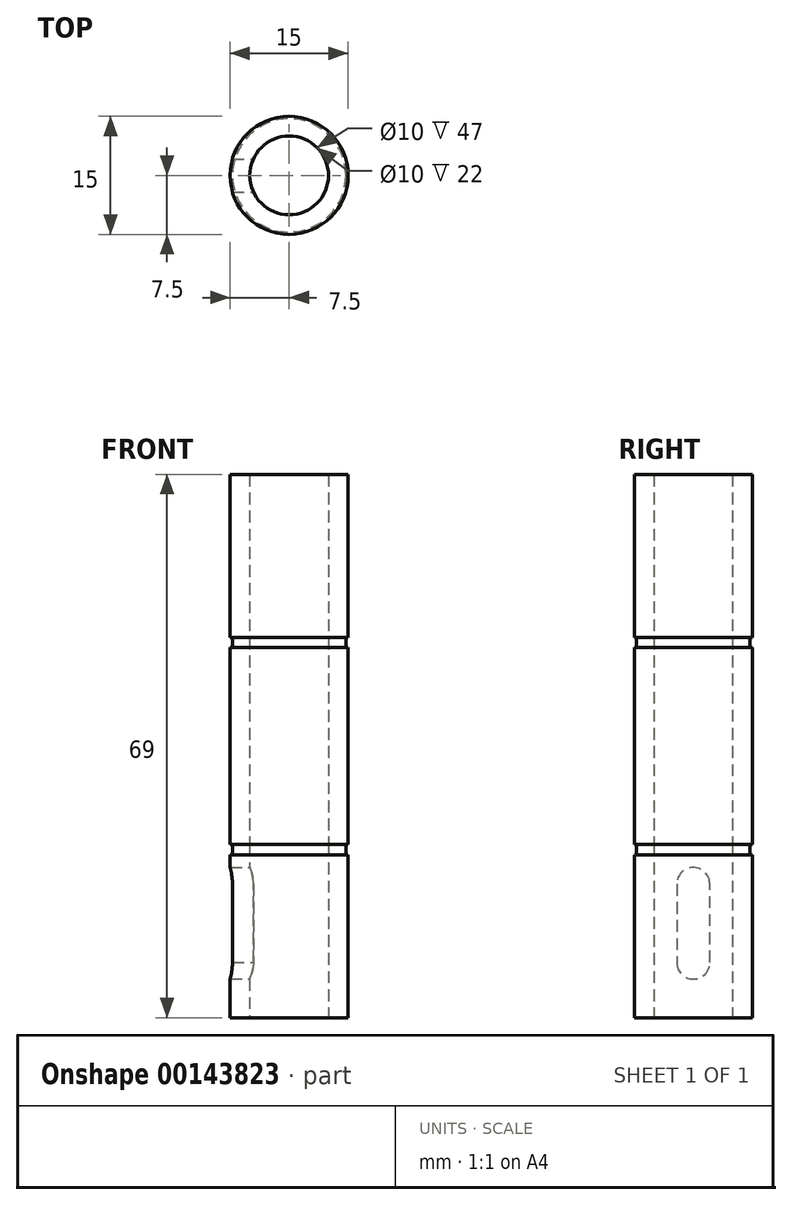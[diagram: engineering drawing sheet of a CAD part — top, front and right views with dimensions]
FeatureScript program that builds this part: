
annotation { "Feature Type Name" : "Feature", "Feature Type Description" : "" }
export const myFeature = defineFeature(function(context is Context, id is Id, definition is map)
    precondition{}
    {
        {
            var Q0;
            Q0=qCreatedBy(makeId("Top.planeOp"),FACE);
            var sketch = newSketch(context, id + "F0", { "sketchPlane" : qUnion([Q0])});
            skCircle(sketch, "E0", {"center": v(0, 0) * mm, "radius": 7.5 * mm});
            skCircle(sketch, "E1", {"center": v(0, 0) * mm, "radius": 5 * mm});
            skSolve(sketch);
        }
        {
            var Q0;
            Q0=makeQuery(id+"F0.imprint","IMPRINT",FACE,{"disambiguationData":[TD([[makeQuery(id+"F0.imprint","IMPRINT",EDGE,{"derivedFrom":sQuery(id+"F0.wireOp",EDGE,"E0")}),1.0]])]});
            extrude(context, id + "F1", {"entities" : qUnion([Q0]), "depth" : 20.7 * mm});
        }
        {
            var Q0;
            Q0=makeQuery(id+"F1.opExtrude","CAP_FACE",FACE,{"disambiguationData":[OSD([sQuery(id+"F0.wireOp",EDGE,"E0"),sQuery(id+"F0.wireOp",EDGE,"E1")])],"isStart":false});
            var sketch = newSketch(context, id + "F2", { "sketchPlane" : qUnion([Q0])});
            skCircle(sketch, "E2", {"center": v(0, 0) * mm, "radius": 7.2 * mm});
            skSolve(sketch);
        }
        {
            var Q0;
            Q0=makeQuery(id+"F2.imprint","IMPRINT",FACE,{"disambiguationData":[TD([[makeQuery(id+"F2.imprint","IMPRINT",EDGE,{"derivedFrom":sQuery(id+"F2.wireOp",EDGE,"E2")}),1.0]])]});
            extrude(context, id + "F3", {"entities" : qUnion([Q0]), "operationType" : NewBodyOperationType.ADD, "depth" : 1.3 * mm});
        }
        {
            var Q0;
            Q0=makeQuery(id+"F3.opExtrude","CAP_FACE",FACE,{"disambiguationData":[OSD([sQuery(id+"F0.wireOp",EDGE,"E1"),sQuery(id+"F2.wireOp",EDGE,"E2")])],"isStart":false});
            var sketch = newSketch(context, id + "F4", { "sketchPlane" : qUnion([Q0])});
            skCircle(sketch, "E3", {"center": v(0, 0) * mm, "radius": 7.5 * mm});
            skSolve(sketch);
        }
        {
            var Q0;
            Q0=makeQuery(id+"F4.imprint","IMPRINT",FACE,{"disambiguationData":[TD([[makeQuery(id+"F4.imprint","IMPRINT",EDGE,{"derivedFrom":sQuery(id+"F4.wireOp",EDGE,"E3")}),1.0]])]});
            var Q1;
            Q1=makeQuery(id+"F4.imprint","IMPRINT",FACE,{"disambiguationData":[TD([[makeQuery(id+"F4.imprint","IMPRINT",EDGE,{"derivedFrom":makeQuery(id+"F3.opExtrude","CAP_EDGE",EDGE,{"disambiguationData":[OSD([sQuery(id+"F2.wireOp",EDGE,"E2")])],"isStart":false})}),1.0]])]});
            extrude(context, id + "F5", {"entities" : qUnion([Q0, Q1]), "depth" : 25 * mm});
        }
        {
            var Q0;
            Q0=makeQuery(id+"F5.opExtrude","CAP_FACE",FACE,{"disambiguationData":[OSD([sQuery(id+"F0.wireOp",EDGE,"E1"),sQuery(id+"F4.wireOp",EDGE,"E3")])],"isStart":false});
            var sketch = newSketch(context, id + "F6", { "sketchPlane" : qUnion([Q0])});
            skCircle(sketch, "E4", {"center": v(0, 0) * mm, "radius": 7.2 * mm});
            skSolve(sketch);
        }
        {
            var Q0;
            Q0=makeQuery(id+"F6.imprint","IMPRINT",FACE,{"disambiguationData":[TD([[makeQuery(id+"F6.imprint","IMPRINT",EDGE,{"derivedFrom":sQuery(id+"F6.wireOp",EDGE,"E4")}),1.0]])]});
            extrude(context, id + "F7", {"entities" : qUnion([Q0]), "operationType" : NewBodyOperationType.ADD, "depth" : 1.3 * mm});
        }
        {
            var Q0;
            Q0=makeQuery(id+"F7.opExtrude","CAP_FACE",FACE,{"disambiguationData":[OSD([sQuery(id+"F0.wireOp",EDGE,"E1"),sQuery(id+"F6.wireOp",EDGE,"E4")])],"isStart":false});
            var sketch = newSketch(context, id + "F8", { "sketchPlane" : qUnion([Q0])});
            skCircle(sketch, "E5", {"center": v(0, 0) * mm, "radius": 7.5 * mm});
            skSolve(sketch);
        }
        {
            var Q0;
            Q0=makeQuery(id+"F8.imprint","IMPRINT",FACE,{"disambiguationData":[TD([[makeQuery(id+"F8.imprint","IMPRINT",EDGE,{"derivedFrom":makeQuery(id+"F7.opExtrude","CAP_EDGE",EDGE,{"disambiguationData":[OSD([sQuery(id+"F6.wireOp",EDGE,"E4")])],"isStart":false})}),1.0]])]});
            var Q1;
            Q1=makeQuery(id+"F8.imprint","IMPRINT",FACE,{"disambiguationData":[TD([[makeQuery(id+"F8.imprint","IMPRINT",EDGE,{"derivedFrom":sQuery(id+"F8.wireOp",EDGE,"E5")}),1.0]])]});
            extrude(context, id + "F9", {"entities" : qUnion([Q0, Q1]), "operationType" : NewBodyOperationType.ADD, "depth" : 20.7 * mm});
        }
        {
            var Q0;
            Q0=qCreatedBy(makeId("Right.planeOp"),FACE);
            var sketch = newSketch(context, id + "F10", { "sketchPlane" : qUnion([Q0])});
            skArc(sketch, "E6", {"start": v(-2.1, 7) * mm, "mid": v(0.02, 4.9) * mm, "end": v(2.1, 7.03) * mm});
            skArc(sketch, "E7", {"start": v(2.1, 17) * mm, "mid": v(0, 19.1) * mm, "end": v(-2.1, 17) * mm});
            skLineSegment(sketch, "E8", {"start": v(-2.1, 7) * mm, "end": v(-2.1, 17) * mm});
            skLineSegment(sketch, "E9", {"start": v(2.1, 6.97) * mm, "end": v(2.1, 17) * mm});
            skSolve(sketch);
        }
        {
            var Q0;
            Q0 = qSketchRegion(id + "F10", true);
            extrude(context, id + "F11", {"entities" : qUnion([Q0]), "operationType" : NewBodyOperationType.REMOVE, "oppositeDirection" : true, "depth" : 7.5 * mm});
        }
    });
